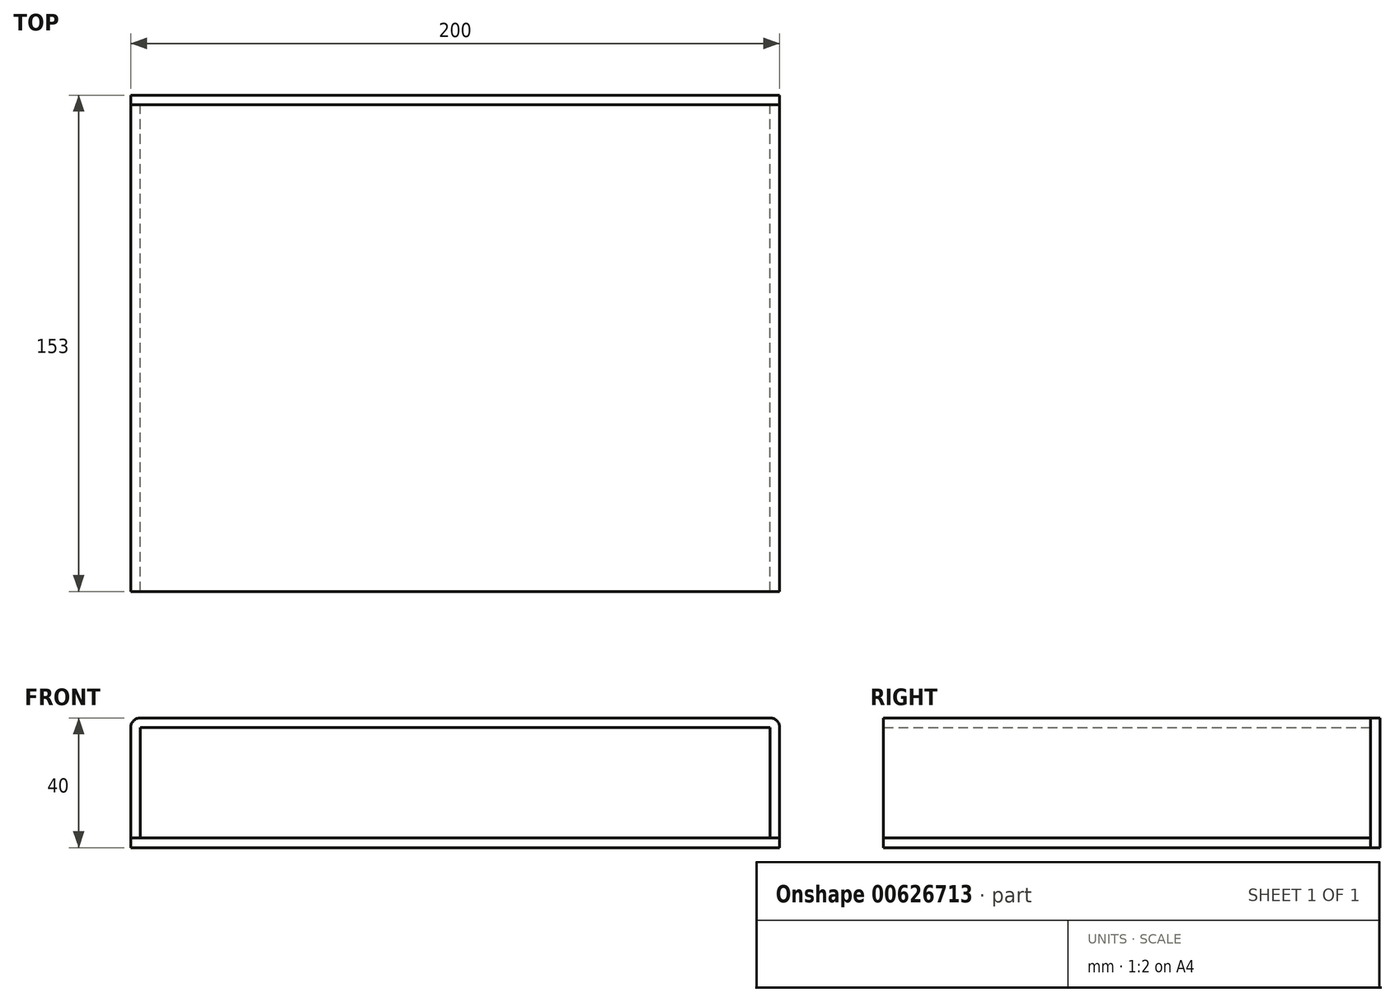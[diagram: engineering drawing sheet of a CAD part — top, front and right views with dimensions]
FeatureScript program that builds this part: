
annotation { "Feature Type Name" : "Feature", "Feature Type Description" : "" }
export const myFeature = defineFeature(function(context is Context, id is Id, definition is map)
    precondition{}
    {
        {
            var Q0;
            Q0=qCreatedBy(makeId("Front.planeOp"),FACE);
            var sketch = newSketch(context, id + "F0", { "sketchPlane" : qUnion([Q0])});
            skLineSegment(sketch, "E0.bottom", {"start": v(97, 18.5) * mm, "end": v(-97, 18.5) * mm});
            skLineSegment(sketch, "E0.left", {"start": v(100, 15.5) * mm, "end": v(100, -18.5) * mm});
            skLineSegment(sketch, "E0.right", {"start": v(-100, 15.5) * mm, "end": v(-100, -18.5) * mm});
            skPoint(sketch, "E0.middle", {"position": v(0, 0) * mm});
            skPoint(sketch, "E1.visualSharp", {"position": v(-100, 18.5) * mm});
            skArc(sketch, "E1.filletArc", {"start": v(-97, 18.5) * mm, "mid": v(-99.12, 17.62) * mm, "end": v(-100, 15.5) * mm});
            skPoint(sketch, "E2.visualSharp", {"position": v(100, 18.5) * mm});
            skArc(sketch, "E2.filletArc", {"start": v(100, 15.5) * mm, "mid": v(99.12, 17.62) * mm, "end": v(97, 18.5) * mm});
            skLineSegment(sketch, "E3.0", {"start": v(97, 15.5) * mm, "end": v(-97, 15.5) * mm});
            skLineSegment(sketch, "E4.0", {"start": v(97, 15.5) * mm, "end": v(97, -18.5) * mm});
            skLineSegment(sketch, "E5.0", {"start": v(-97, 15.5) * mm, "end": v(-97, -18.5) * mm});
            skLineSegment(sketch, "E6", {"start": v(97, -18.5) * mm, "end": v(100, -18.5) * mm});
            skLineSegment(sketch, "E7", {"start": v(-97, -18.5) * mm, "end": v(-100, -18.5) * mm});
            skSolve(sketch);
        }
        {
            var Q0;
            Q0=makeQuery(id+"F0.imprint","IMPRINT",FACE,{"disambiguationData":[TD([[makeQuery(id+"F0.imprint","IMPRINT",EDGE,{"derivedFrom":sQuery(id+"F0.wireOp",EDGE,"E0.bottom")}),1.0]])]});
            extrude(context, id + "F1", {"entities" : qUnion([Q0]), "depth" : (150 / 2) * mm, "offsetDistance" : 25 * mm, "hasSecondDirection" : true, "secondDirectionOppositeDirection" : true, "secondDirectionDepth" : (150 / 2) * mm});
        }
        {
            var Q0;
            Q0=makeQuery(id+"F1.opExtrude","SWEPT_FACE",FACE,{"disambiguationData":[OSD([sQuery(id+"F0.wireOp",EDGE,"E0.bottom")])]});
            cPlane(context, id + "F2", {"entities" : qUnion([Q0]), "cplaneType" : CPlaneType.OFFSET, "offset" : 37 * mm, "oppositeDirection" : true, "width" : 150 * mm, "height" : 150 * mm});
        }
        {
            var Q0;
            Q0=qCreatedBy(id+"F2.planeOp",FACE);
            var sketch = newSketch(context, id + "F3", { "sketchPlane" : qUnion([Q0])});
            skLineSegment(sketch, "E8.bottom", {"start": v(100, -75) * mm, "end": v(-100, -75) * mm});
            skLineSegment(sketch, "E8.top", {"start": v(100, 75) * mm, "end": v(-100, 75) * mm});
            skLineSegment(sketch, "E8.left", {"start": v(100, -75) * mm, "end": v(100, 75) * mm});
            skLineSegment(sketch, "E8.right", {"start": v(-100, -75) * mm, "end": v(-100, 75) * mm});
            skPoint(sketch, "E8.middle", {"position": v(0, 0) * mm});
            skSolve(sketch);
        }
        {
            var Q0;
            Q0=makeQuery(id+"F3.imprint","IMPRINT",FACE,{"disambiguationData":[TD([[makeQuery(id+"F3.imprint","IMPRINT",EDGE,{"derivedFrom":sQuery(id+"F3.wireOp",EDGE,"E8.bottom")}),-1.0]])]});
            extrude(context, id + "F4", {"entities" : qUnion([Q0]), "oppositeDirection" : true, "depth" : 3 * mm, "offsetDistance" : 25 * mm});
        }
        {
            var Q0;
            Q0=qCreatedBy(makeId("Front.planeOp"),FACE);
            cPlane(context, id + "F5", {"entities" : qUnion([Q0]), "cplaneType" : CPlaneType.OFFSET, "offset" : (150 / 2) * mm, "oppositeDirection" : true, "width" : 150 * mm, "height" : 150 * mm});
        }
        {
            var Q0;
            Q0=qCreatedBy(id+"F5.planeOp",FACE);
            var sketch = newSketch(context, id + "F6", { "sketchPlane" : qUnion([Q0])});
            skLineSegment(sketch, "E9.bottom", {"start": v(97, 18.5) * mm, "end": v(-97, 18.5) * mm});
            skLineSegment(sketch, "E9.top", {"start": v(100, -21.5) * mm, "end": v(-100, -21.5) * mm});
            skLineSegment(sketch, "E9.left", {"start": v(100, 15.5) * mm, "end": v(100, -21.5) * mm});
            skLineSegment(sketch, "E9.right", {"start": v(-100, 15.5) * mm, "end": v(-100, -21.5) * mm});
            skPoint(sketch, "E10.visualSharp", {"position": v(100, 18.5) * mm});
            skArc(sketch, "E10.filletArc", {"start": v(100, 15.5) * mm, "mid": v(99.12, 17.62) * mm, "end": v(97, 18.5) * mm});
            skPoint(sketch, "E11.visualSharp", {"position": v(-100, 18.5) * mm});
            skArc(sketch, "E11.filletArc", {"start": v(-97, 18.5) * mm, "mid": v(-99.12, 17.62) * mm, "end": v(-100, 15.5) * mm});
            skSolve(sketch);
        }
        {
            var Q0;
            Q0 = qSketchRegion(id + "F6", true);
            extrude(context, id + "F7", {"entities" : qUnion([Q0]), "oppositeDirection" : true, "depth" : 3 * mm, "offsetDistance" : 25 * mm});
        }
    });
